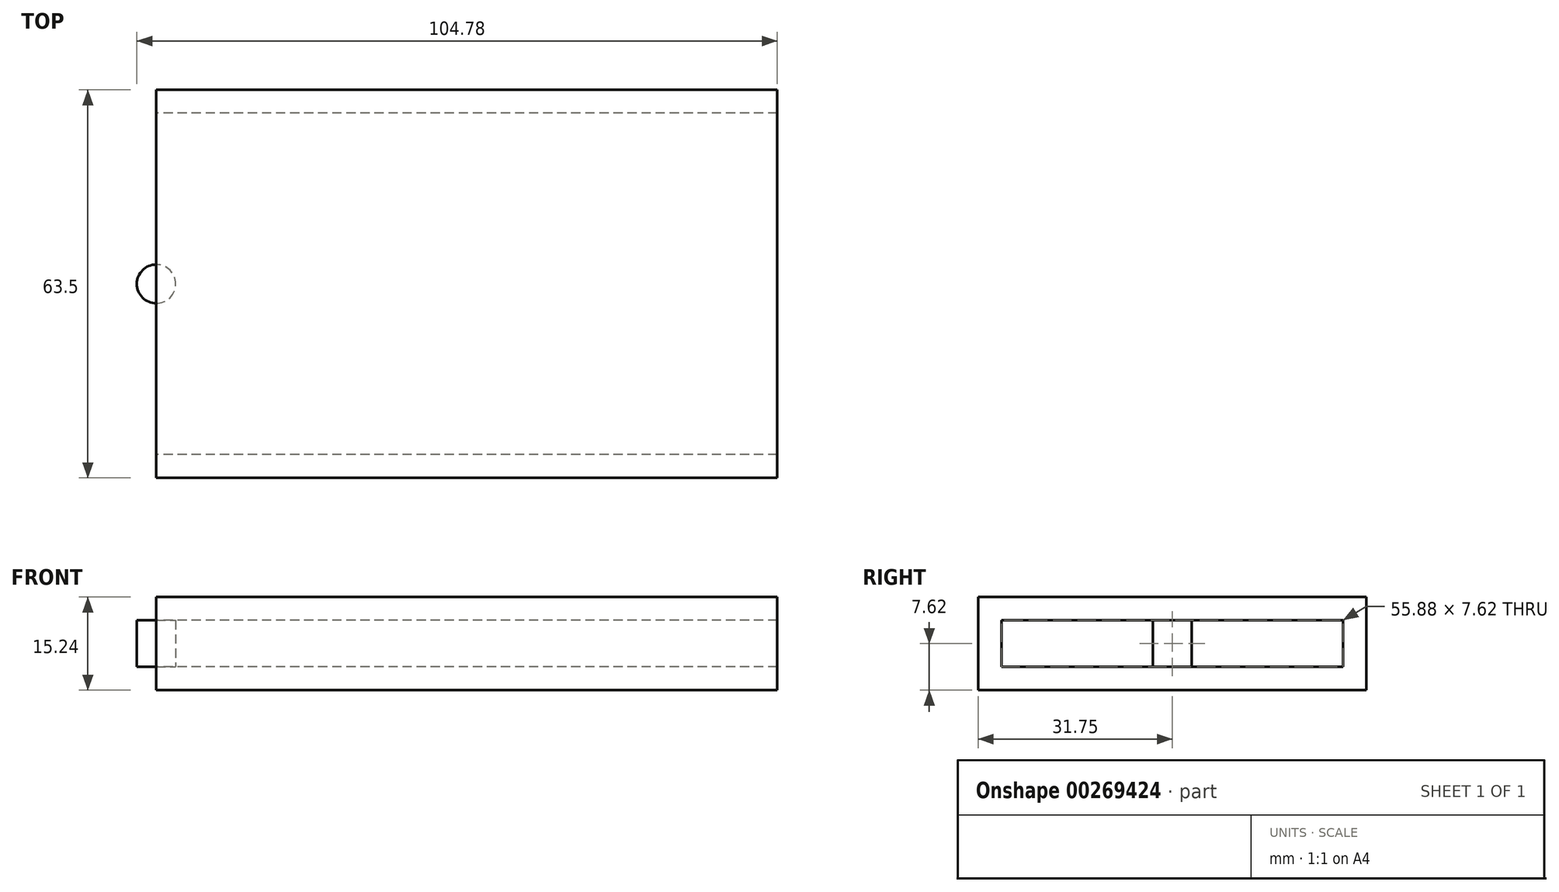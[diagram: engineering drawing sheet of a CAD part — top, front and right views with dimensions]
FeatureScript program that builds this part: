
annotation { "Feature Type Name" : "Feature", "Feature Type Description" : "" }
export const myFeature = defineFeature(function(context is Context, id is Id, definition is map)
    precondition{}
    {
        {
            var Q0;
            Q0=qCreatedBy(makeId("Right.planeOp"),FACE);
            var sketch = newSketch(context, id + "F0", { "sketchPlane" : qUnion([Q0])});
            skLineSegment(sketch, "E0.top", {"start": v(31.75, 7.62) * mm, "end": v(27.94, 7.62) * mm});
            skLineSegment(sketch, "E0.left", {"start": v(31.75, -7.62) * mm, "end": v(31.75, 7.62) * mm});
            skLineSegment(sketch, "E0.right", {"start": v(27.94, -3.8) * mm, "end": v(27.94, 7.62) * mm});
            skLineSegment(sketch, "E1.MirrorCS", {"start": v(-31.75, -7.62) * mm, "end": v(-31.75, 7.62) * mm});
            skLineSegment(sketch, "E2.MirrorCS", {"start": v(-27.94, -3.8) * mm, "end": v(-27.94, 7.62) * mm});
            skLineSegment(sketch, "E3.MirrorCS", {"start": v(-31.75, 7.62) * mm, "end": v(-27.94, 7.62) * mm});
            skLineSegment(sketch, "E4.bottom", {"start": v(31.75, 7.62) * mm, "end": v(-31.75, 7.62) * mm});
            skLineSegment(sketch, "E4.top", {"start": v(31.75, 3.8) * mm, "end": v(-31.75, 3.8) * mm});
            skLineSegment(sketch, "E4.left", {"start": v(31.75, 7.62) * mm, "end": v(31.75, 3.8) * mm});
            skLineSegment(sketch, "E4.right", {"start": v(-31.75, 7.62) * mm, "end": v(-31.75, 3.8) * mm});
            skLineSegment(sketch, "E5.MirrorCS", {"start": v(31.75, -7.62) * mm, "end": v(27.94, -7.62) * mm});
            skLineSegment(sketch, "E6.MirrorCS", {"start": v(31.75, -7.62) * mm, "end": v(31.75, -3.8) * mm});
            skLineSegment(sketch, "E7.MirrorCS", {"start": v(-31.75, -7.62) * mm, "end": v(-31.75, -3.8) * mm});
            skLineSegment(sketch, "E8.MirrorCS", {"start": v(31.75, -3.8) * mm, "end": v(-31.75, -3.8) * mm});
            skLineSegment(sketch, "E9.MirrorCS", {"start": v(31.75, -7.62) * mm, "end": v(-31.75, -7.62) * mm});
            skSolve(sketch);
        }
        {
            var Q0;
            Q0 = qSketchRegion(id + "F0", true);
            extrude(context, id + "F1", {"entities" : qUnion([Q0]), "depth" : 101.6 * mm});
        }
        {
            var Q0;
            Q0=makeQuery(id+"F1.opExtrude","SWEPT_FACE",FACE,{"disambiguationData":[OSD([sQuery(id+"F0.wireOp",EDGE,"E8.MirrorCS")])]});
            var sketch = newSketch(context, id + "F2", { "sketchPlane" : qUnion([Q0])});
            skCircle(sketch, "E10", {"center": v(0, 0) * mm, "radius": 3.18 * mm});
            skSolve(sketch);
        }
        {
            var Q0;
            Q0 = qSketchRegion(id + "F2", true);
            extrude(context, id + "F3", {"entities" : qUnion([Q0]), "operationType" : NewBodyOperationType.ADD, "depth" : 7.62 * mm});
        }
    });
